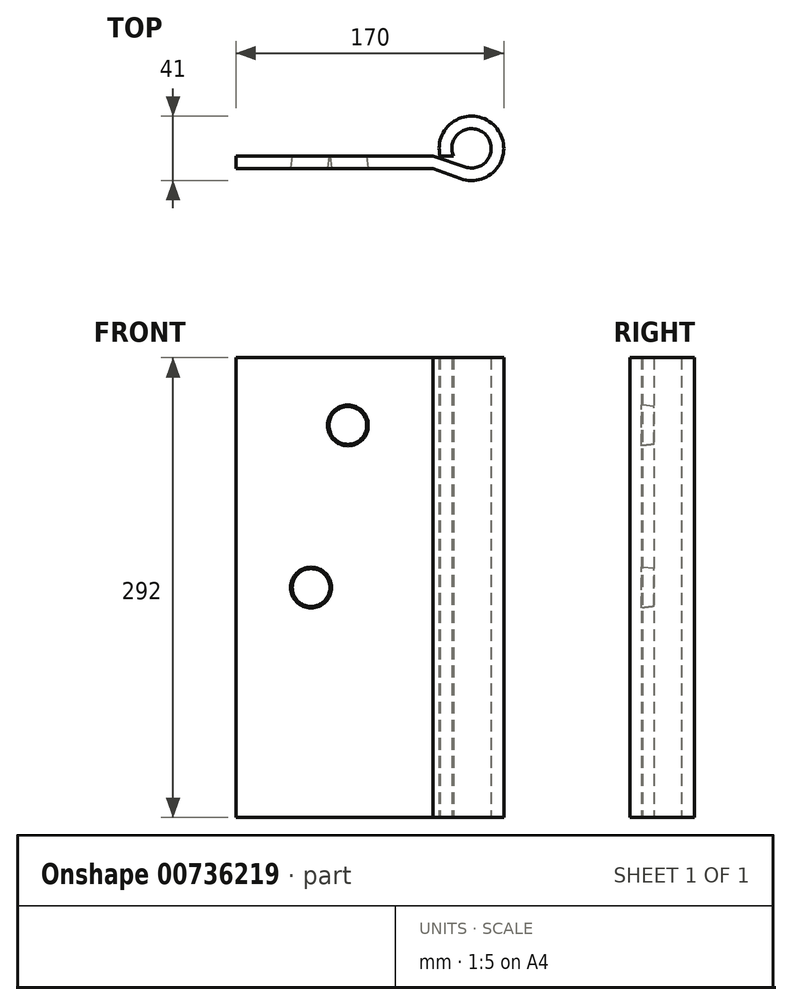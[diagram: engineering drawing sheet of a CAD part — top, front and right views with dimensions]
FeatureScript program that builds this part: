
annotation { "Feature Type Name" : "Feature", "Feature Type Description" : "" }
export const myFeature = defineFeature(function(context is Context, id is Id, definition is map)
    precondition{}
    {
        {
            var Q0;
            Q0=qCreatedBy(makeId("Top.planeOp"),FACE);
            var sketch = newSketch(context, id + "F0", { "sketchPlane" : qUnion([Q0])});
            skLineSegment(sketch, "E0", {"start": v(0, 0) * mm, "end": v(-125, 0) * mm});
            skLineSegment(sketch, "E1", {"start": v(-125, 0) * mm, "end": v(-125, -8) * mm});
            skLineSegment(sketch, "E2", {"start": v(-125, -8) * mm, "end": v(0, -8) * mm});
            skArc(sketch, "E3", {"start": v(20.54, -6.86) * mm, "mid": v(32.94, 14.22) * mm, "end": v(13.04, 0) * mm});
            skArc(sketch, "E4", {"start": v(17.59, -14.3) * mm, "mid": v(39.69, 18.77) * mm, "end": v(4.62, 0) * mm});
            skLineSegment(sketch, "E5", {"start": v(4.62, 0) * mm, "end": v(13.04, 0) * mm});
            skLineSegment(sketch, "E6", {"start": v(0, 0) * mm, "end": v(20.54, -6.86) * mm});
            skLineSegment(sketch, "E7", {"start": v(0, -8) * mm, "end": v(17.59, -14.3) * mm});
            skSolve(sketch);
        }
        {
            var Q0;
            Q0 = qSketchRegion(id + "F0", true);
            extrude(context, id + "F1", {"entities" : qUnion([Q0]), "depth" : 292 * mm, "offsetDistance" : 25.4 * mm});
        }
        {
            var Q0;
            Q0=makeQuery(id+"F1.opExtrude","SWEPT_FACE",FACE,{"disambiguationData":[OSD([sQuery(id+"F0.wireOp",EDGE,"E2")])]});
            var sketch = newSketch(context, id + "F2", { "sketchPlane" : qUnion([Q0])});
            skCircle(sketch, "E8", {"center": v(-54.03, 249.03) * mm, "radius": 12.97 * mm});
            skLineSegment(sketch, "E9", {"start": v(-125, 146) * mm, "end": v(0, 146) * mm, "construction": true});
            skCircle(sketch, "E10", {"center": v(-77.38, 146) * mm, "radius": 12.98 * mm});
            skCircle(sketch, "E11.MirrorC", {"center": v(-54.03, 42.97) * mm, "radius": 12.97 * mm});
            skSolve(sketch);
        }
        {
            var Q0;
            Q0=qCreatedBy(makeId("Front.planeOp"),FACE);
            var sketch = newSketch(context, id + "F3", { "sketchPlane" : qUnion([Q0])});
            skPoint(sketch, "E12.0", {"position": v(-54.03, 249.03) * mm});
            skPoint(sketch, "E13.0", {"position": v(-77.38, 146) * mm});
            skPoint(sketch, "E14.0", {"position": v(-54.03, 42.97) * mm});
            skCircle(sketch, "E15", {"center": v(-54.03, 249.03) * mm, "radius": 12 * mm});
            skCircle(sketch, "E16", {"center": v(-77.38, 146) * mm, "radius": 12 * mm});
            skCircle(sketch, "E17", {"center": v(-54.03, 42.97) * mm, "radius": 12 * mm});
            skSolve(sketch);
        }
        {
            var Q1;
            Q1=makeQuery(id+"F3.imprint","IMPRINT",FACE,{"disambiguationData":[TD([[makeQuery(id+"F3.imprint","IMPRINT",EDGE,{"derivedFrom":sQuery(id+"F3.wireOp",EDGE,"E15")}),1.0]])]});
            var Q2;
            Q2=makeQuery(id+"F2.imprint","IMPRINT",FACE,{"disambiguationData":[TD([[makeQuery(id+"F2.imprint","IMPRINT",EDGE,{"derivedFrom":sQuery(id+"F2.wireOp",EDGE,"E8")}),1.0]])]});
            loft(context, id + "F4", {"operationType" : NewBodyOperationType.REMOVE, "sheetProfilesArray" : [{ "sheetProfileEntities" : qUnion([Q1]) }, { "sheetProfileEntities" : qUnion([Q2]) }]});
        }
        {
            var Q1;
            Q1=makeQuery(id+"F2.imprint","IMPRINT",FACE,{"disambiguationData":[TD([[makeQuery(id+"F2.imprint","IMPRINT",EDGE,{"derivedFrom":sQuery(id+"F2.wireOp",EDGE,"E10")}),1.0]])]});
            var Q2;
            Q2=makeQuery(id+"F3.imprint","IMPRINT",FACE,{"disambiguationData":[TD([[makeQuery(id+"F3.imprint","IMPRINT",EDGE,{"derivedFrom":sQuery(id+"F3.wireOp",EDGE,"E16")}),1.0]])]});
            loft(context, id + "F5", {"operationType" : NewBodyOperationType.REMOVE, "sheetProfilesArray" : [{ "sheetProfileEntities" : qUnion([Q1]) }, { "sheetProfileEntities" : qUnion([Q2]) }]});
        }
    });
